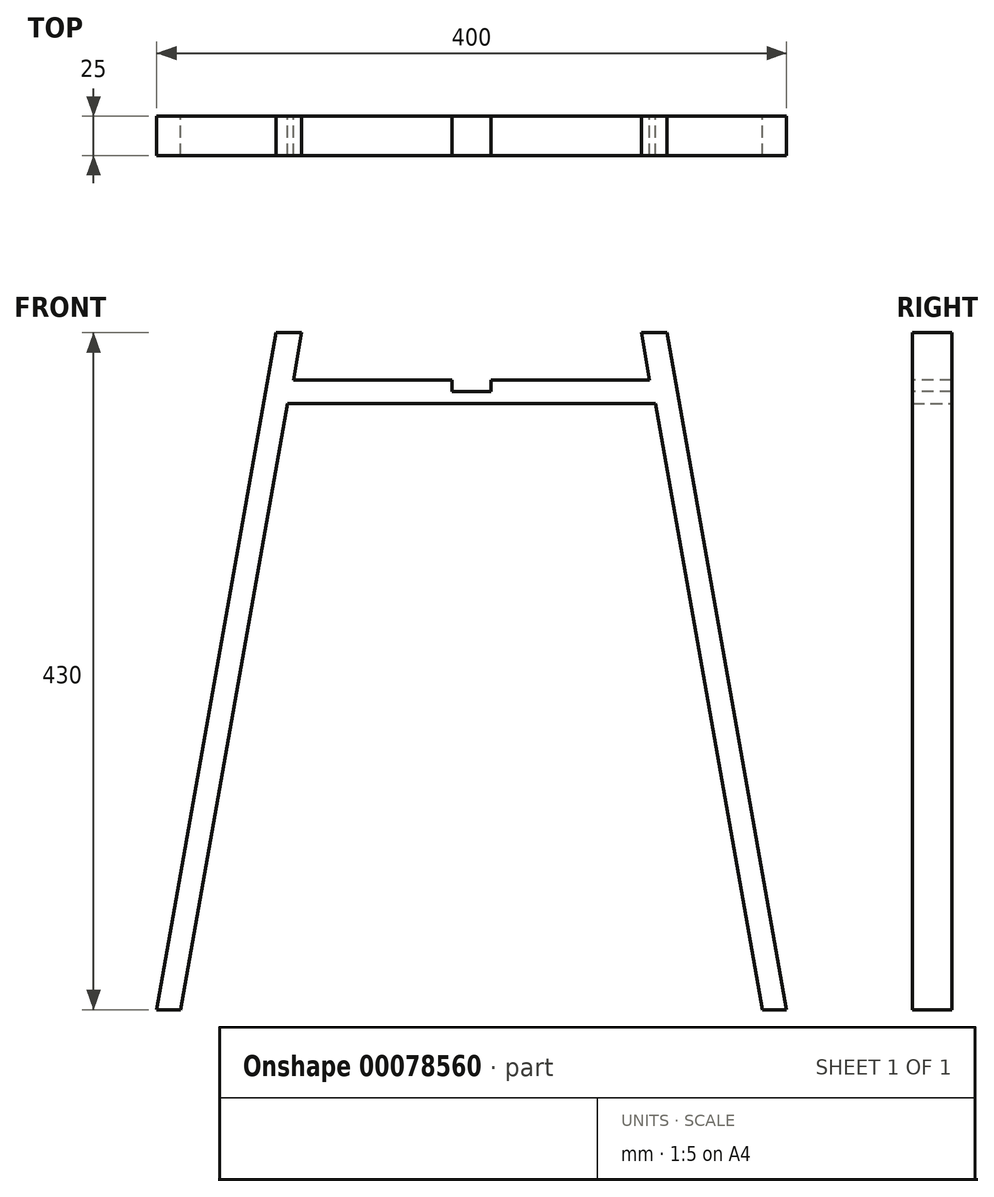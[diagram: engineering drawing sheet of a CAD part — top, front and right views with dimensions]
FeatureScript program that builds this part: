
annotation { "Feature Type Name" : "Feature", "Feature Type Description" : "" }
export const myFeature = defineFeature(function(context is Context, id is Id, definition is map)
    precondition{}
    {
        {
            var Q0;
            Q0=qCreatedBy(makeId("Front.planeOp"),FACE);
            var sketch = newSketch(context, id + "F0", { "sketchPlane" : qUnion([Q0])});
            skLineSegment(sketch, "E0", {"start": v(0, 385) * mm, "end": v(-116.88, 385) * mm});
            skLineSegment(sketch, "E1", {"start": v(-116.88, 385) * mm, "end": v(-184.77, 0) * mm});
            skLineSegment(sketch, "E2", {"start": v(-184.77, 0) * mm, "end": v(-200, 0) * mm});
            skLineSegment(sketch, "E3", {"start": v(-200, 0) * mm, "end": v(-124.18, 430) * mm});
            skLineSegment(sketch, "E4", {"start": v(-124.18, 430) * mm, "end": v(-107.82, 430) * mm});
            skLineSegment(sketch, "E5", {"start": v(-107.82, 430) * mm, "end": v(-113.11, 400) * mm});
            skLineSegment(sketch, "E6", {"start": v(-113.11, 400) * mm, "end": v(0, 400) * mm});
            skLineSegment(sketch, "E7", {"start": v(0, 400) * mm, "end": v(0, 385) * mm});
            skLineSegment(sketch, "E8.MirrorCS", {"start": v(107.82, 430) * mm, "end": v(113.11, 400) * mm});
            skLineSegment(sketch, "E9.MirrorCS", {"start": v(124.18, 430) * mm, "end": v(107.82, 430) * mm});
            skLineSegment(sketch, "E10.MirrorCS", {"start": v(184.77, 0) * mm, "end": v(200, 0) * mm});
            skLineSegment(sketch, "E11.MirrorCS", {"start": v(116.88, 385) * mm, "end": v(184.77, 0) * mm});
            skLineSegment(sketch, "E12.MirrorCS", {"start": v(113.11, 400) * mm, "end": v(0, 400) * mm});
            skLineSegment(sketch, "E13.MirrorCS", {"start": v(200, 0) * mm, "end": v(124.18, 430) * mm});
            skLineSegment(sketch, "E14.MirrorCS", {"start": v(0, 385) * mm, "end": v(116.88, 385) * mm});
            skSolve(sketch);
        }
        {
            var Q0;
            Q0 = qSketchRegion(id + "F0", true);
            extrude(context, id + "F1", {"entities" : qUnion([Q0]), "endBound" : BoundingType.SYMMETRIC, "depth" : 25 * mm});
        }
        {
            var Q0;
            Q0=qCreatedBy(makeId("Front.planeOp"),FACE);
            var sketch = newSketch(context, id + "F2", { "sketchPlane" : qUnion([Q0])});
            skLineSegment(sketch, "E15", {"start": v(0, -22.46) * mm, "end": v(0, 481.86) * mm, "construction": true});
            skLineSegment(sketch, "E16.bottom", {"start": v(12.5, 400) * mm, "end": v(-12.5, 400) * mm});
            skLineSegment(sketch, "E16.top", {"start": v(12.5, 392.5) * mm, "end": v(-12.5, 392.5) * mm});
            skLineSegment(sketch, "E16.left", {"start": v(12.5, 400) * mm, "end": v(12.5, 392.5) * mm});
            skLineSegment(sketch, "E16.right", {"start": v(-12.5, 400) * mm, "end": v(-12.5, 392.5) * mm});
            skSolve(sketch);
        }
        {
            var Q0;
            Q0 = qSketchRegion(id + "F2", true);
            extrude(context, id + "F3", {"entities" : qUnion([Q0]), "operationType" : NewBodyOperationType.REMOVE, "endBound" : BoundingType.SYMMETRIC, "oppositeDirection" : true, "depth" : 25 * mm});
        }
    });
